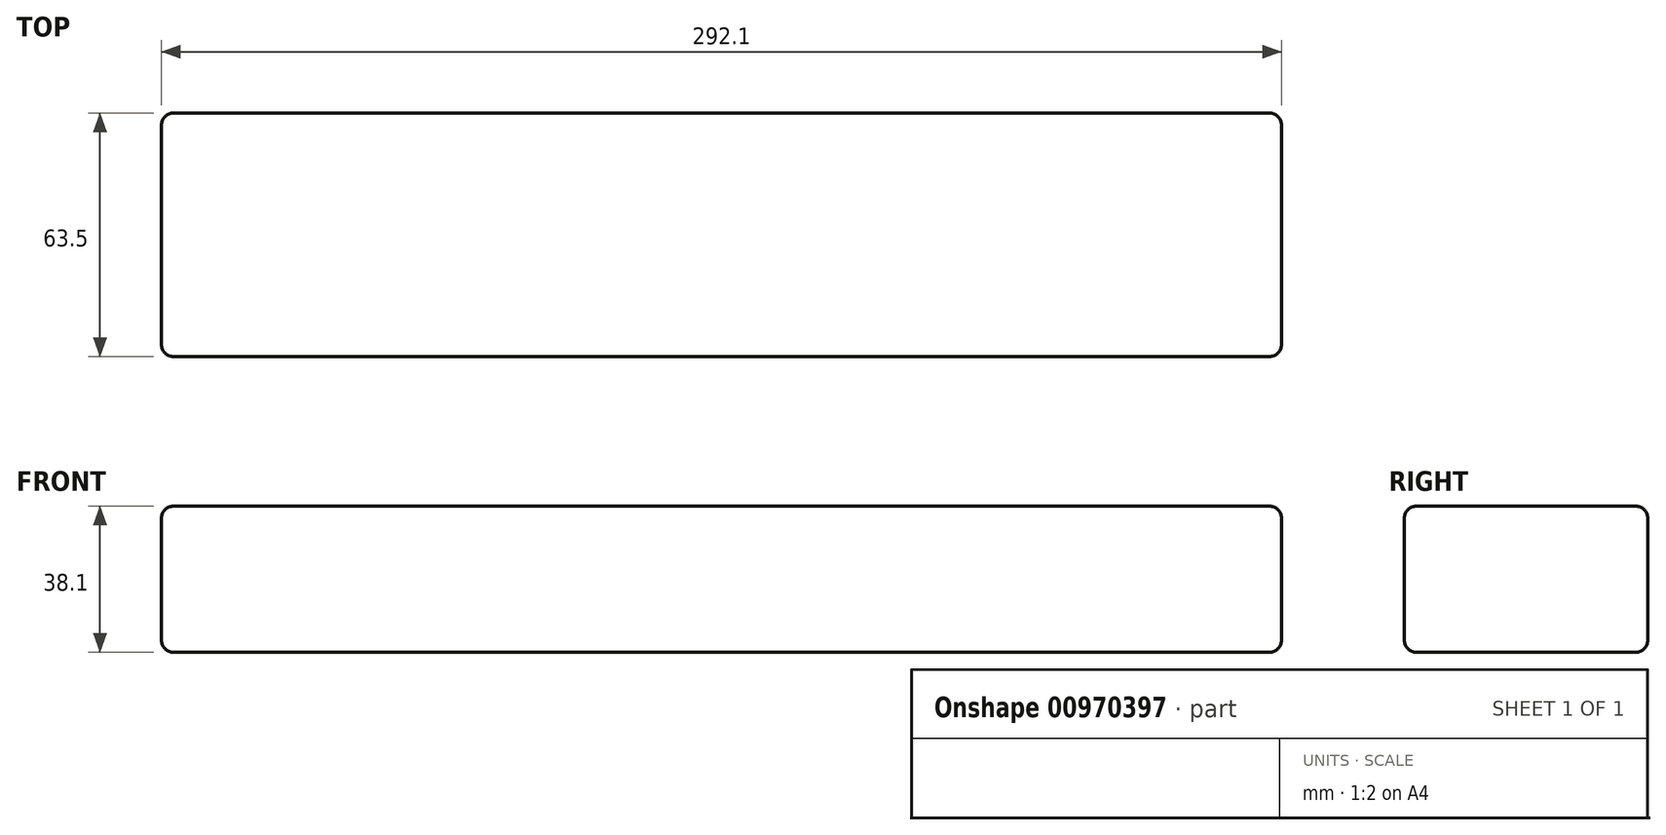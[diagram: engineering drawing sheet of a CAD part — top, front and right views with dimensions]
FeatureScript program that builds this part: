
annotation { "Feature Type Name" : "Feature", "Feature Type Description" : "" }
export const myFeature = defineFeature(function(context is Context, id is Id, definition is map)
    precondition{}
    {
        {
            var Q0;
            Q0=qCreatedBy(makeId("Front.planeOp"),FACE);
            var sketch = newSketch(context, id + "F0", { "sketchPlane" : qUnion([Q0])});
            skLineSegment(sketch, "E0.bottom", {"start": v(0, 0) * mm, "end": v(292.1, 0) * mm});
            skLineSegment(sketch, "E0.top", {"start": v(0, -38.1) * mm, "end": v(292.1, -38.1) * mm});
            skLineSegment(sketch, "E0.left", {"start": v(0, 0) * mm, "end": v(0, -38.1) * mm});
            skLineSegment(sketch, "E0.right", {"start": v(292.1, 0) * mm, "end": v(292.1, -38.1) * mm});
            skSolve(sketch);
        }
        {
            var Q0;
            Q0 = qSketchRegion(id + "F0", true);
            extrude(context, id + "F1", {"entities" : qUnion([Q0]), "depth" : 63.5 * mm, "offsetDistance" : 25.4 * mm});
        }
        {
            var Q0;
            Q0=makeQuery(id+"F1.opExtrude","CAP_EDGE",EDGE,{"disambiguationData":[OSD([sQuery(id+"F0.wireOp",EDGE,"E0.top")])],"isStart":false});
            var Q1;
            Q1=makeQuery(id+"F1.opExtrude","CAP_EDGE",EDGE,{"disambiguationData":[OSD([sQuery(id+"F0.wireOp",EDGE,"E0.left")])],"isStart":true});
            var Q2;
            Q2=makeQuery(id+"F1.opExtrude","CAP_EDGE",EDGE,{"disambiguationData":[OSD([sQuery(id+"F0.wireOp",EDGE,"E0.left")])],"isStart":false});
            var Q3;
            Q3=makeQuery(id+"F1.opExtrude","CAP_EDGE",EDGE,{"disambiguationData":[OSD([sQuery(id+"F0.wireOp",EDGE,"E0.bottom")])],"isStart":false});
            var Q4;
            Q4=makeQuery(id+"F1.opExtrude","SWEPT_EDGE",EDGE,{"disambiguationData":[OSD([sQuery(id+"F0.wireOp",EDGE,"E0.bottom"),sQuery(id+"F0.wireOp",EDGE,"E0.left")])]});
            var Q5;
            Q5=makeQuery(id+"F1.opExtrude","CAP_EDGE",EDGE,{"disambiguationData":[OSD([sQuery(id+"F0.wireOp",EDGE,"E0.bottom")])],"isStart":true});
            var Q6;
            Q6=makeQuery(id+"F1.opExtrude","SWEPT_EDGE",EDGE,{"disambiguationData":[OSD([sQuery(id+"F0.wireOp",EDGE,"E0.top"),sQuery(id+"F0.wireOp",EDGE,"E0.left")])]});
            var Q7;
            Q7=makeQuery(id+"F1.opExtrude","SWEPT_EDGE",EDGE,{"disambiguationData":[OSD([sQuery(id+"F0.wireOp",EDGE,"E0.bottom"),sQuery(id+"F0.wireOp",EDGE,"E0.right")])]});
            var Q8;
            Q8=makeQuery(id+"F1.opExtrude","SWEPT_EDGE",EDGE,{"disambiguationData":[OSD([sQuery(id+"F0.wireOp",EDGE,"E0.top"),sQuery(id+"F0.wireOp",EDGE,"E0.right")])]});
            var Q9;
            Q9=makeQuery(id+"F1.opExtrude","CAP_EDGE",EDGE,{"disambiguationData":[OSD([sQuery(id+"F0.wireOp",EDGE,"E0.right")])],"isStart":true});
            var Q10;
            Q10=makeQuery(id+"F1.opExtrude","CAP_EDGE",EDGE,{"disambiguationData":[OSD([sQuery(id+"F0.wireOp",EDGE,"E0.right")])],"isStart":false});
            var Q11;
            Q11=makeQuery(id+"F1.opExtrude","CAP_EDGE",EDGE,{"disambiguationData":[OSD([sQuery(id+"F0.wireOp",EDGE,"E0.top")])],"isStart":true});
            fillet(context, id + "F2", {"entities" : qUnion([Q0, Q1, Q2, Q3, Q4, Q5, Q6, Q7, Q8, Q9, Q10, Q11]), "radius" : 3.17 * mm, "tangentPropagation" : true, "allowEdgeOverflow" : false});
        }
    });
